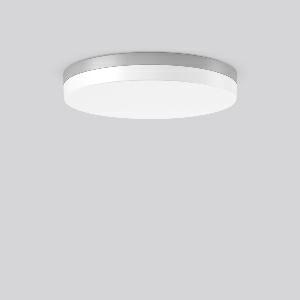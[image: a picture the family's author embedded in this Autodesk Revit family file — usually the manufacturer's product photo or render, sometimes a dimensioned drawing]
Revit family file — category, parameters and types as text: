
# Revit family: flat_slim_round_312677_004_19_58e6
name_source: partatom
category: Lighting Fixtures
units: mm (PartAtom-declared; Revit-internal decimal feet)

## family parameters
Cut with Voids When Loaded = No
Host = Face
Light Source = No
Part Type = Normal
Room Calculation Point = No
Round Connector Dimension = Use Diameter
Shared = No

## types (1)
- MultiLumen 1 830 (1 x LED Modul 830, 3350 lm, 3000)
    Apparent Load = 31 VA
    CIE Flux Codes = 41 71 90 86 100
    Color Rendering = 80
    Color Temperature = 3000
    Default Elevation = 1800 mm
    Height = 75 mm
    Lamp = 1 x LED Modul 830
    Lamp Light Flux = 3350 lm
    Lamp count = 1
    Length = 480 mm
    Lifetime = 50000 h
    Luminous efficacy = 108 lm/W
    Manufacturer = RZB
    ModVariant = No
    Model = 312677.004.19
    Mounting Place = Ceiling
    Mounting Type = Surface mounted
    Number of Poles = 1
    OnlyDefault = Yes
    Power Factor = 1
    Product Name = FLAT SLIM round
    Product group = Surface mounted ceiling and wall luminaires
    ProductGroupID = 305
    Protection Class = Protection class I
    Protection Degree = Degree of protection
    RLX_Detail_Level = 1
    RLX_Emergency_Light_Flux = 0 lm
    RLX_Emergency_Type = 0
    RLX_Emergency_Type_DB = No
    RlxData = <blob elided: 22289 chars, md5=9e3df0fc>
    Socket = socket
    Standby Power = 0 W
    System Light Flux = 3350 lm
    System Power = 31 W
    Type Comments = MultiLumen 1 830
    Type Image = 312633.004.jpg
    URL = http://relux.com
    VarID = multilumen_1_830
    Voltage = 0 V
    Weight = 0.00 kg
    Width = 0 mm  [stored 0 ft]

note: [stored X ft] marks values corroborated as IEEE doubles in the binary element streams (Revit-internal decimal feet)

## geometry (parser evidence)
native form markers: Blend x4, Sweep x15
no freeform markers — native parametric forms only
